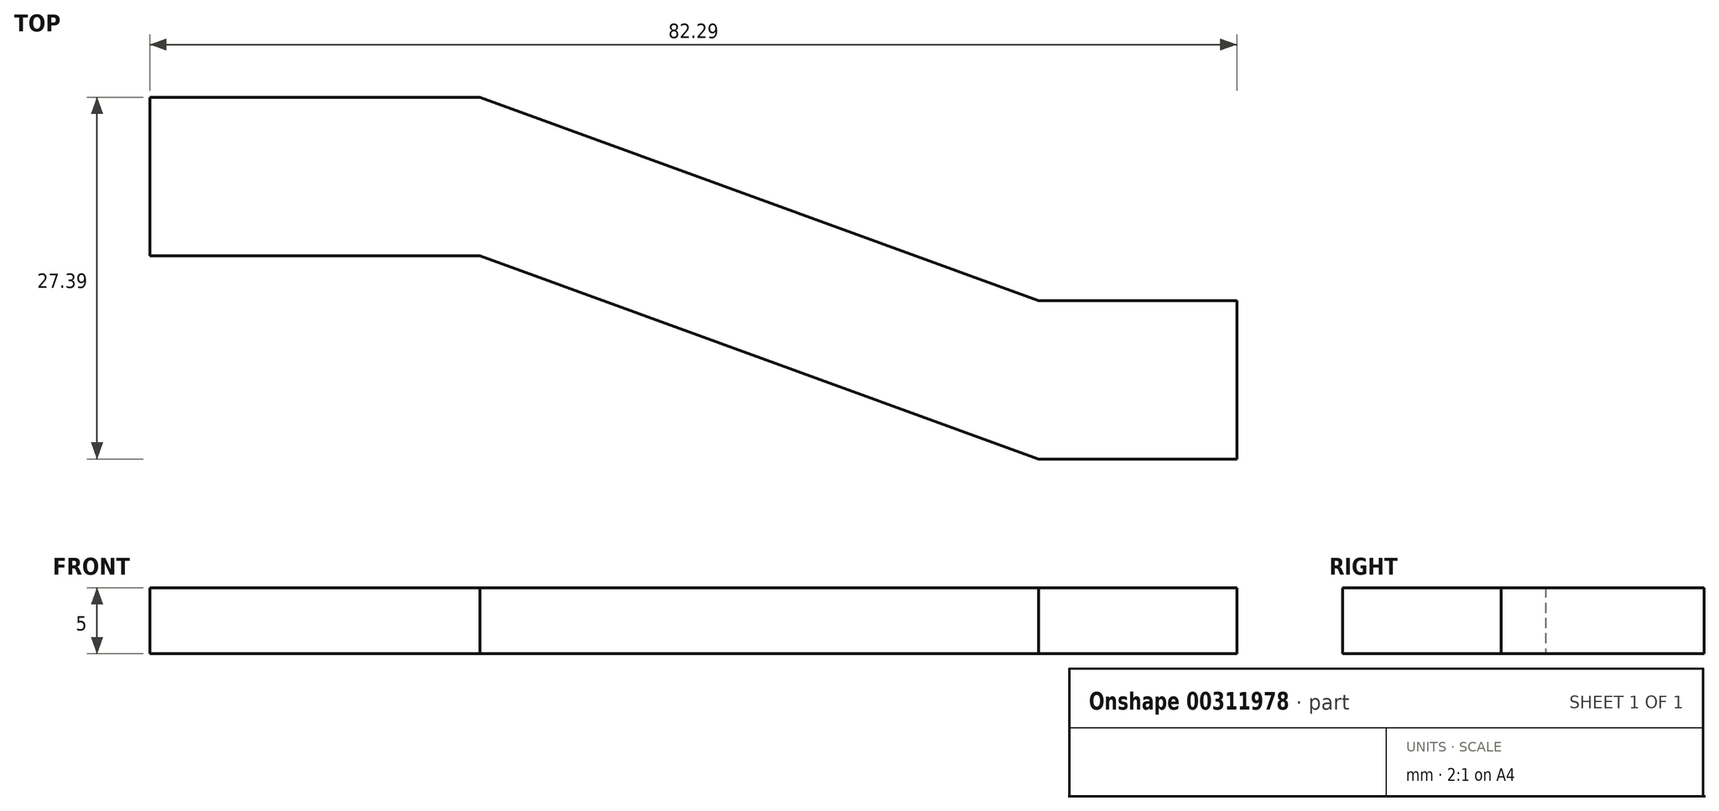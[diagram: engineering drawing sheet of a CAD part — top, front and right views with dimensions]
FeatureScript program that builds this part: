
annotation { "Feature Type Name" : "Feature", "Feature Type Description" : "" }
export const myFeature = defineFeature(function(context is Context, id is Id, definition is map)
    precondition{}
    {
        {
            var Q0;
            Q0=qCreatedBy(makeId("Top.planeOp"),FACE);
            var sketch = newSketch(context, id + "F0", { "sketchPlane" : qUnion([Q0])});
            skLineSegment(sketch, "E0.bottom", {"start": v(0, 12) * mm, "end": v(25, 12) * mm});
            skLineSegment(sketch, "E0.top", {"start": v(0, 0) * mm, "end": v(25, 0) * mm});
            skLineSegment(sketch, "E0.left", {"start": v(0, 12) * mm, "end": v(0, 0) * mm});
            skLineSegment(sketch, "E0.right", {"start": v(25, 12) * mm, "end": v(25, 0) * mm});
            skLineSegment(sketch, "E1.bottom", {"start": v(67.29, -3.4) * mm, "end": v(82.29, -3.4) * mm});
            skLineSegment(sketch, "E1.top", {"start": v(67.29, -15.4) * mm, "end": v(82.29, -15.4) * mm});
            skLineSegment(sketch, "E1.left", {"start": v(67.29, -3.4) * mm, "end": v(67.29, -15.4) * mm});
            skLineSegment(sketch, "E1.right", {"start": v(82.29, -3.4) * mm, "end": v(82.29, -15.4) * mm});
            skLineSegment(sketch, "E2", {"start": v(25, 0) * mm, "end": v(67.29, -15.4) * mm});
            skLineSegment(sketch, "E3", {"start": v(25, 12) * mm, "end": v(67.29, -3.4) * mm});
            skSolve(sketch);
        }
        {
            var Q0;
            Q0=makeQuery(id+"F0.imprint","IMPRINT",FACE,{"disambiguationData":[TD([[makeQuery(id+"F0.imprint","IMPRINT",EDGE,{"derivedFrom":sQuery(id+"F0.wireOp",EDGE,"E0.bottom")}),-1.0]])]});
            var Q1;
            Q1=makeQuery(id+"F0.imprint","IMPRINT",FACE,{"disambiguationData":[TD([[makeQuery(id+"F0.imprint","IMPRINT",EDGE,{"derivedFrom":sQuery(id+"F0.wireOp",EDGE,"E0.right")}),1.0]])]});
            var Q2;
            Q2=makeQuery(id+"F0.imprint","IMPRINT",FACE,{"disambiguationData":[TD([[makeQuery(id+"F0.imprint","IMPRINT",EDGE,{"derivedFrom":sQuery(id+"F0.wireOp",EDGE,"E1.bottom")}),-1.0]])]});
            extrude(context, id + "F1", {"entities" : qUnion([Q0, Q1, Q2]), "depth" : 5 * mm});
        }
    });
